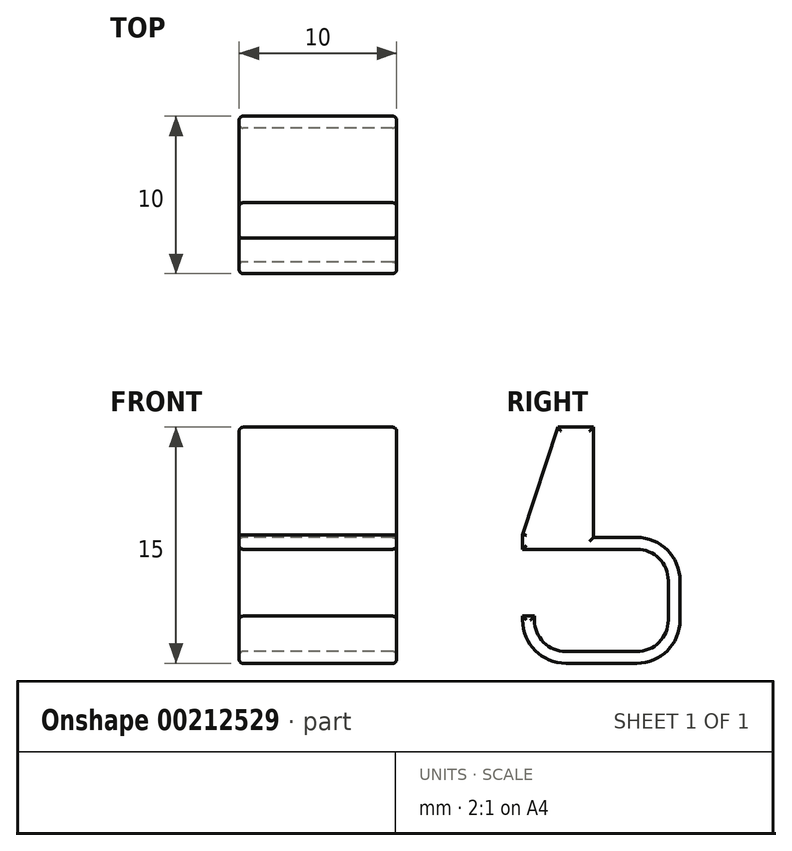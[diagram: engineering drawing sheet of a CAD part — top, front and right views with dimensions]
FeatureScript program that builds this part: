
annotation { "Feature Type Name" : "Feature", "Feature Type Description" : "" }
export const myFeature = defineFeature(function(context is Context, id is Id, definition is map)
    precondition{}
    {
        {
            var Q0;
            Q0=qCreatedBy(makeId("Right.planeOp"),FACE);
            var sketch = newSketch(context, id + "F0", { "sketchPlane" : qUnion([Q0])});
            skLineSegment(sketch, "E0", {"start": v(-16.38, 27.16) * mm, "end": v(-16.38, 29.66) * mm});
            skLineSegment(sketch, "E1", {"start": v(-18.38, 31.66) * mm, "end": v(-25.63, 31.66) * mm});
            skLineSegment(sketch, "E2", {"start": v(-25.63, 31.66) * mm, "end": v(-25.63, 32.58) * mm});
            skLineSegment(sketch, "E3", {"start": v(-23.38, 39.4) * mm, "end": v(-21.13, 39.4) * mm});
            skLineSegment(sketch, "E4", {"start": v(-21.13, 39.4) * mm, "end": v(-21.13, 32.4) * mm});
            skLineSegment(sketch, "E5", {"start": v(-21.13, 32.4) * mm, "end": v(-18.38, 32.4) * mm});
            skLineSegment(sketch, "E6", {"start": v(-15.63, 32.4) * mm, "end": v(-15.63, 24.4) * mm, "construction": true});
            skLineSegment(sketch, "E7", {"start": v(-15.63, 29.66) * mm, "end": v(-15.63, 27.16) * mm});
            skLineSegment(sketch, "E8", {"start": v(-25.63, 27.16) * mm, "end": v(-25.63, 27.4) * mm});
            skLineSegment(sketch, "E9", {"start": v(-25.63, 27.4) * mm, "end": v(-24.88, 27.4) * mm});
            skLineSegment(sketch, "E10", {"start": v(-24.88, 27.4) * mm, "end": v(-24.88, 27.16) * mm});
            skLineSegment(sketch, "E11", {"start": v(-22.88, 25.16) * mm, "end": v(-18.38, 25.16) * mm});
            skLineSegment(sketch, "E12", {"start": v(-22.88, 24.4) * mm, "end": v(-18.38, 24.4) * mm});
            skLineSegment(sketch, "E13", {"start": v(-23.38, 39.4) * mm, "end": v(-25.63, 32.58) * mm});
            skPoint(sketch, "E14.orphan", {"position": v(-25.63, 39.4) * mm});
            skPoint(sketch, "E15.visualSharp", {"position": v(-24.88, 25.16) * mm});
            skArc(sketch, "E15.filletArc", {"start": v(-24.88, 27.16) * mm, "mid": v(-24.3, 25.74) * mm, "end": v(-22.88, 25.16) * mm});
            skPoint(sketch, "E16.visualSharp", {"position": v(-16.38, 25.16) * mm});
            skArc(sketch, "E16.filletArc", {"start": v(-18.38, 25.16) * mm, "mid": v(-16.96, 25.74) * mm, "end": v(-16.38, 27.16) * mm});
            skPoint(sketch, "E17.visualSharp", {"position": v(-16.38, 31.66) * mm});
            skArc(sketch, "E17.filletArc", {"start": v(-16.38, 29.66) * mm, "mid": v(-16.96, 31.07) * mm, "end": v(-18.38, 31.66) * mm});
            skPoint(sketch, "E18.visualSharp", {"position": v(-25.63, 24.4) * mm});
            skArc(sketch, "E18.filletArc", {"start": v(-25.63, 27.16) * mm, "mid": v(-24.82, 25.21) * mm, "end": v(-22.88, 24.4) * mm});
            skPoint(sketch, "E19.visualSharp", {"position": v(-15.63, 24.4) * mm});
            skArc(sketch, "E19.filletArc", {"start": v(-18.38, 24.4) * mm, "mid": v(-16.43, 25.21) * mm, "end": v(-15.63, 27.16) * mm});
            skPoint(sketch, "E20.visualSharp", {"position": v(-15.63, 32.4) * mm});
            skArc(sketch, "E20.filletArc", {"start": v(-15.63, 29.66) * mm, "mid": v(-16.43, 31.6) * mm, "end": v(-18.38, 32.4) * mm});
            skSolve(sketch);
        }
        {
            var Q0;
            Q0=makeQuery(id+"F0.imprint","IMPRINT",FACE,{"disambiguationData":[TD([[makeQuery(id+"F0.imprint","IMPRINT",EDGE,{"derivedFrom":sQuery(id+"F0.wireOp",EDGE,"E0")}),-1.0]])]});
            extrude(context, id + "F1", {"entities" : qUnion([Q0]), "depth" : 10 * mm});
        }
        {
            var Q0;
            Q0=makeQuery(id+"F1.opExtrude","CAP_FACE",FACE,{"disambiguationData":[OSD([sQuery(id+"F0.wireOp",EDGE,"E0"),sQuery(id+"F0.wireOp",EDGE,"E1"),sQuery(id+"F0.wireOp",EDGE,"E2"),sQuery(id+"F0.wireOp",EDGE,"E3"),sQuery(id+"F0.wireOp",EDGE,"E4"),sQuery(id+"F0.wireOp",EDGE,"E5"),sQuery(id+"F0.wireOp",EDGE,"E7"),sQuery(id+"F0.wireOp",EDGE,"E8"),sQuery(id+"F0.wireOp",EDGE,"E9"),sQuery(id+"F0.wireOp",EDGE,"E10"),sQuery(id+"F0.wireOp",EDGE,"E11"),sQuery(id+"F0.wireOp",EDGE,"E12"),sQuery(id+"F0.wireOp",EDGE,"E13"),sQuery(id+"F0.wireOp",EDGE,"E15.filletArc"),sQuery(id+"F0.wireOp",EDGE,"E16.filletArc"),sQuery(id+"F0.wireOp",EDGE,"E17.filletArc"),sQuery(id+"F0.wireOp",EDGE,"E18.filletArc"),sQuery(id+"F0.wireOp",EDGE,"E19.filletArc"),sQuery(id+"F0.wireOp",EDGE,"E20.filletArc")])],"isStart":false});
            var Q1;
            Q1=makeQuery(id+"F1.opExtrude","CAP_FACE",FACE,{"disambiguationData":[OSD([sQuery(id+"F0.wireOp",EDGE,"E0"),sQuery(id+"F0.wireOp",EDGE,"E1"),sQuery(id+"F0.wireOp",EDGE,"E2"),sQuery(id+"F0.wireOp",EDGE,"E3"),sQuery(id+"F0.wireOp",EDGE,"E4"),sQuery(id+"F0.wireOp",EDGE,"E5"),sQuery(id+"F0.wireOp",EDGE,"E7"),sQuery(id+"F0.wireOp",EDGE,"E8"),sQuery(id+"F0.wireOp",EDGE,"E9"),sQuery(id+"F0.wireOp",EDGE,"E10"),sQuery(id+"F0.wireOp",EDGE,"E11"),sQuery(id+"F0.wireOp",EDGE,"E12"),sQuery(id+"F0.wireOp",EDGE,"E13"),sQuery(id+"F0.wireOp",EDGE,"E15.filletArc"),sQuery(id+"F0.wireOp",EDGE,"E16.filletArc"),sQuery(id+"F0.wireOp",EDGE,"E17.filletArc"),sQuery(id+"F0.wireOp",EDGE,"E18.filletArc"),sQuery(id+"F0.wireOp",EDGE,"E19.filletArc"),sQuery(id+"F0.wireOp",EDGE,"E20.filletArc")])],"isStart":true});
            fillet(context, id + "F2", {"entities" : qUnion([Q0, Q1]), "radius" : .25 * mm, "tangentPropagation" : true, "allowEdgeOverflow" : false});
        }
    });
